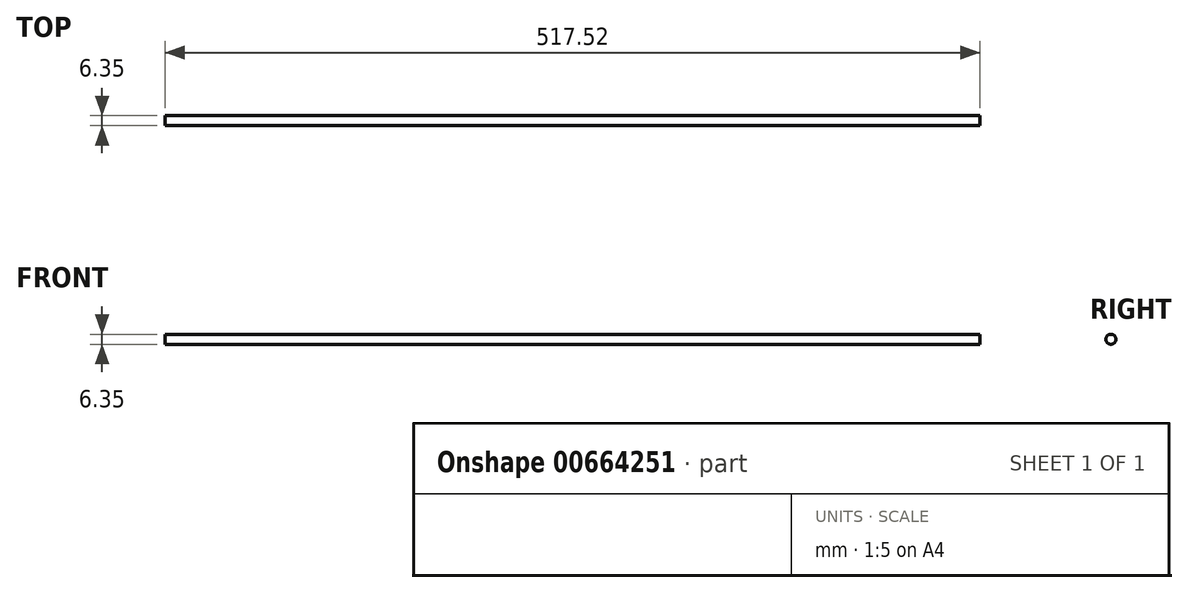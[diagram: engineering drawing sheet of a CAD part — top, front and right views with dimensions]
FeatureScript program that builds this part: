
annotation { "Feature Type Name" : "Feature", "Feature Type Description" : "" }
export const myFeature = defineFeature(function(context is Context, id is Id, definition is map)
    precondition{}
    {
        {
            var Q0;
            Q0=qCreatedBy(makeId("Right.planeOp"),FACE);
            var sketch = newSketch(context, id + "F0", { "sketchPlane" : qUnion([Q0])});
            skCircle(sketch, "E0", {"center": v(92.28, -27.56) * mm, "radius": 3.18 * mm});
            skSolve(sketch);
        }
        {
            var Q0;
            Q0 = qSketchRegion(id + "F0", true);
            extrude(context, id + "F1", {"entities" : qUnion([Q0]), "depth" : 517.52 * mm, "offsetDistance" : 25.4 * mm, "symmetric" : true});
        }
    });
